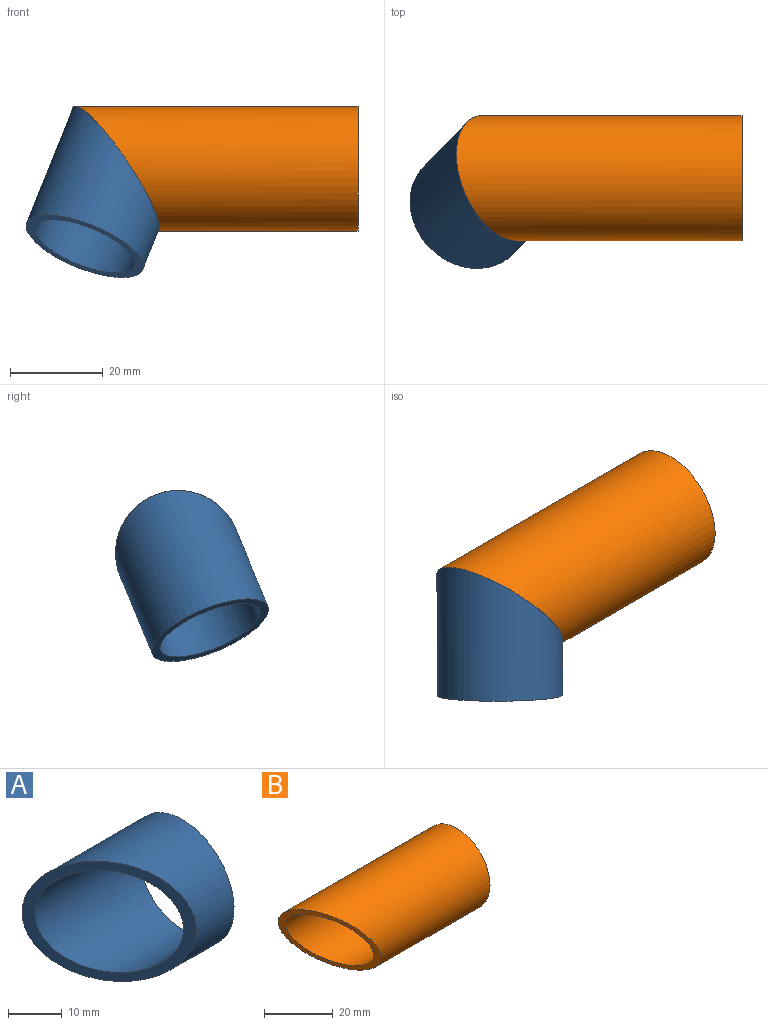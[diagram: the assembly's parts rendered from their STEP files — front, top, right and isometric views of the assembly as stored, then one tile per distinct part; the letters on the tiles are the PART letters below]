
ASSEMBLY  parts=2 mates=1
PART A: 4 faces, bbox 28.6x27x27 mm
  f0: cylinder r=11.5mm len=27.24mm, axis (-1,0,0), area 1391mm2, adj f2,f3
  f1: cylinder r=13.5mm len=28.63mm, axis (-1,0,0), area 1632.9mm2, adj f2,f3
  f2: plane 27x27mm, normal (1,0,0), area 157.1mm2, adj f0,f1
  f3: plane 27x27mm, normal (-0.82,-0.57,0), area 191.2mm2, adj f0,f1
PART B: 4 faces, bbox 61.7x27x27 mm
  f0: cylinder r=11.5mm len=60.28mm, axis (-1,0,0), area 3777.9mm2, adj f2,f3
  f1: cylinder r=13.5mm len=61.67mm, axis (-1,0,0), area 4435mm2, adj f2,f3
  f2: plane 27x27mm, normal (1,0,0), area 157.1mm2, adj f0,f1
  f3: plane 27x27mm, normal (-0.82,-0.4,-0.4), area 191.2mm2, adj f0,f1
PLACE A rot(axis=(-0.5,0.72,0.48),143deg) t=(-30.2,-20.32,9.7)mm
PLACE B rot(axis=(1,0,0),22.5deg) t=(-42.85,-23.68,1.59)mm
MATE fastened A.f3 <-> B.f3  axis (0.82,0.22,0.53) through (-33.47,-23.68,1.59)mm
